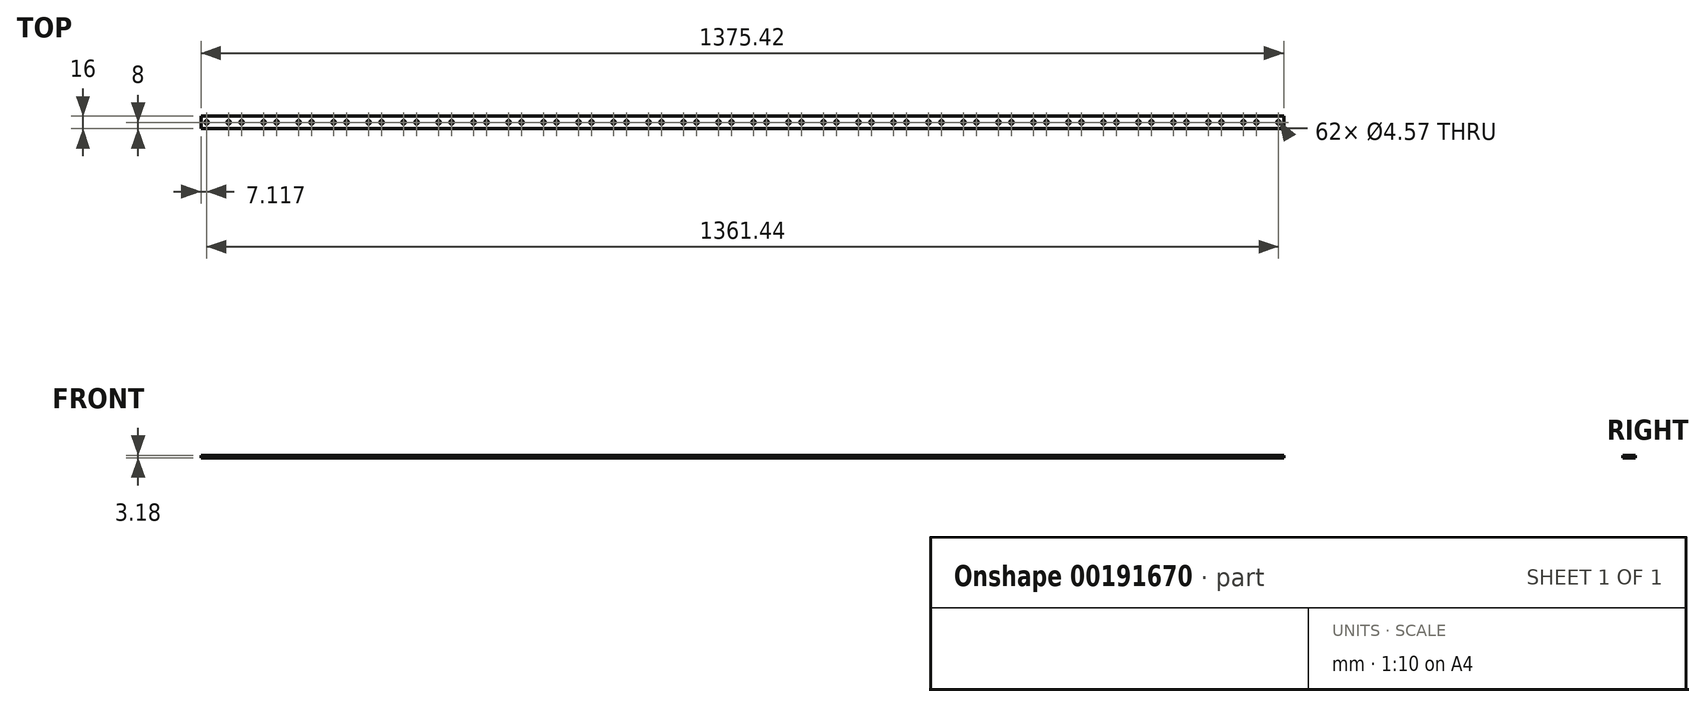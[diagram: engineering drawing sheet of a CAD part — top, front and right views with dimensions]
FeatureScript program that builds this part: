
annotation { "Feature Type Name" : "Feature", "Feature Type Description" : "" }
export const myFeature = defineFeature(function(context is Context, id is Id, definition is map)
    precondition{}
    {
        {
            var Q0;
            Q0=qCreatedBy(makeId("Top.planeOp"),FACE);
            var sketch = newSketch(context, id + "F0", { "sketchPlane" : qUnion([Q0])});
            skLineSegment(sketch, "E0.bottom", {"start": v(-687.7, 8) * mm, "end": v(687.7, 8) * mm});
            skLineSegment(sketch, "E0.top", {"start": v(-687.7, -8) * mm, "end": v(687.7, -8) * mm});
            skLineSegment(sketch, "E0.left", {"start": v(-687.7, 8) * mm, "end": v(-687.7, -8) * mm});
            skLineSegment(sketch, "E0.right", {"start": v(687.7, 8) * mm, "end": v(687.7, -8) * mm});
            skPoint(sketch, "E0.middle", {"position": v(0, 0) * mm});
            skLineSegment(sketch, "E1", {"start": v(-760.01, 0) * mm, "end": v(731.19, 0) * mm, "construction": true});
            skLineSegment(sketch, "E2.0", {"start": v(-680.6, 8) * mm, "end": v(-680.6, -8) * mm, "construction": true});
            skLineSegment(sketch, "E3.0", {"start": v(-652.65, 8) * mm, "end": v(-652.65, -8) * mm, "construction": true});
            skCircle(sketch, "E4", {"center": v(-680.6, 0) * mm, "radius": 2.29 * mm});
            skCircle(sketch, "E5", {"center": v(-652.65, 0) * mm, "radius": 2.29 * mm});
            skCircle(sketch, "E6.1.0.0", {"center": v(-636.14, 0) * mm, "radius": 2.29 * mm});
            skLineSegment(sketch, "E6.direction1", {"start": v(-652.65, 0) * mm, "end": v(-636.14, 0) * mm, "construction": true});
            skCircle(sketch, "E7.1.0.0", {"center": v(-608.2, 0) * mm, "radius": 2.29 * mm});
            skLineSegment(sketch, "E7.direction1", {"start": v(-636.14, 0) * mm, "end": v(-608.2, 0) * mm, "construction": true});
            skCircle(sketch, "E8.1.0.0", {"center": v(-591.7, 0) * mm, "radius": 2.29 * mm});
            skCircle(sketch, "E8.1.0.1", {"center": v(-563.75, 0) * mm, "radius": 2.29 * mm});
            skLineSegment(sketch, "E8.1.0.2", {"start": v(-591.7, 0) * mm, "end": v(-563.75, 0) * mm, "construction": true});
            skCircle(sketch, "E8.2.0.0", {"center": v(-547.24, 0) * mm, "radius": 2.29 * mm});
            skCircle(sketch, "E8.2.0.1", {"center": v(-519.3, 0) * mm, "radius": 2.29 * mm});
            skLineSegment(sketch, "E8.2.0.2", {"start": v(-547.24, 0) * mm, "end": v(-519.3, 0) * mm, "construction": true});
            skCircle(sketch, "E8.3.0.0", {"center": v(-502.8, 0) * mm, "radius": 2.29 * mm});
            skCircle(sketch, "E8.3.0.1", {"center": v(-474.85, 0) * mm, "radius": 2.29 * mm});
            skLineSegment(sketch, "E8.3.0.2", {"start": v(-502.8, 0) * mm, "end": v(-474.85, 0) * mm, "construction": true});
            skCircle(sketch, "E8.4.0.0", {"center": v(-458.34, 0) * mm, "radius": 2.29 * mm});
            skCircle(sketch, "E8.4.0.1", {"center": v(-430.4, 0) * mm, "radius": 2.29 * mm});
            skLineSegment(sketch, "E8.4.0.2", {"start": v(-458.34, 0) * mm, "end": v(-430.4, 0) * mm, "construction": true});
            skCircle(sketch, "E8.5.0.0", {"center": v(-413.9, 0) * mm, "radius": 2.29 * mm});
            skCircle(sketch, "E8.5.0.1", {"center": v(-385.95, 0) * mm, "radius": 2.29 * mm});
            skLineSegment(sketch, "E8.5.0.2", {"start": v(-413.9, 0) * mm, "end": v(-385.95, 0) * mm, "construction": true});
            skCircle(sketch, "E8.6.0.0", {"center": v(-369.44, 0) * mm, "radius": 2.29 * mm});
            skCircle(sketch, "E8.6.0.1", {"center": v(-341.5, 0) * mm, "radius": 2.29 * mm});
            skLineSegment(sketch, "E8.6.0.2", {"start": v(-369.44, 0) * mm, "end": v(-341.5, 0) * mm, "construction": true});
            skCircle(sketch, "E8.7.0.0", {"center": v(-325, 0) * mm, "radius": 2.29 * mm});
            skCircle(sketch, "E8.7.0.1", {"center": v(-297.05, 0) * mm, "radius": 2.29 * mm});
            skLineSegment(sketch, "E8.7.0.2", {"start": v(-325, 0) * mm, "end": v(-297.05, 0) * mm, "construction": true});
            skCircle(sketch, "E8.8.0.0", {"center": v(-280.54, 0) * mm, "radius": 2.29 * mm});
            skCircle(sketch, "E8.8.0.1", {"center": v(-252.6, 0) * mm, "radius": 2.29 * mm});
            skLineSegment(sketch, "E8.8.0.2", {"start": v(-280.54, 0) * mm, "end": v(-252.6, 0) * mm, "construction": true});
            skCircle(sketch, "E8.9.0.0", {"center": v(-236.1, 0) * mm, "radius": 2.29 * mm});
            skCircle(sketch, "E8.9.0.1", {"center": v(-208.15, 0) * mm, "radius": 2.29 * mm});
            skLineSegment(sketch, "E8.9.0.2", {"start": v(-236.1, 0) * mm, "end": v(-208.15, 0) * mm, "construction": true});
            skCircle(sketch, "E8.10.0.0", {"center": v(-191.64, 0) * mm, "radius": 2.29 * mm});
            skCircle(sketch, "E8.10.0.1", {"center": v(-163.7, 0) * mm, "radius": 2.29 * mm});
            skLineSegment(sketch, "E8.10.0.2", {"start": v(-191.64, 0) * mm, "end": v(-163.7, 0) * mm, "construction": true});
            skCircle(sketch, "E8.11.0.0", {"center": v(-147.2, 0) * mm, "radius": 2.29 * mm});
            skCircle(sketch, "E8.11.0.1", {"center": v(-119.25, 0) * mm, "radius": 2.29 * mm});
            skLineSegment(sketch, "E8.11.0.2", {"start": v(-147.2, 0) * mm, "end": v(-119.25, 0) * mm, "construction": true});
            skCircle(sketch, "E8.12.0.0", {"center": v(-102.74, 0) * mm, "radius": 2.29 * mm});
            skCircle(sketch, "E8.12.0.1", {"center": v(-74.8, 0) * mm, "radius": 2.29 * mm});
            skLineSegment(sketch, "E8.12.0.2", {"start": v(-102.74, 0) * mm, "end": v(-74.8, 0) * mm, "construction": true});
            skCircle(sketch, "E8.13.0.0", {"center": v(-58.3, 0) * mm, "radius": 2.29 * mm});
            skCircle(sketch, "E8.13.0.1", {"center": v(-30.35, 0) * mm, "radius": 2.29 * mm});
            skLineSegment(sketch, "E8.13.0.2", {"start": v(-58.3, 0) * mm, "end": v(-30.35, 0) * mm, "construction": true});
            skCircle(sketch, "E8.14.0.0", {"center": v(-13.84, 0) * mm, "radius": 2.29 * mm});
            skCircle(sketch, "E8.14.0.1", {"center": v(14.1, 0) * mm, "radius": 2.29 * mm});
            skLineSegment(sketch, "E8.14.0.2", {"start": v(-13.84, 0) * mm, "end": v(14.1, 0) * mm, "construction": true});
            skCircle(sketch, "E8.15.0.0", {"center": v(30.6, 0) * mm, "radius": 2.29 * mm});
            skCircle(sketch, "E8.15.0.1", {"center": v(58.55, 0) * mm, "radius": 2.29 * mm});
            skLineSegment(sketch, "E8.15.0.2", {"start": v(30.6, 0) * mm, "end": v(58.55, 0) * mm, "construction": true});
            skCircle(sketch, "E8.16.0.0", {"center": v(75.06, 0) * mm, "radius": 2.29 * mm});
            skCircle(sketch, "E8.16.0.1", {"center": v(103, 0) * mm, "radius": 2.29 * mm});
            skLineSegment(sketch, "E8.16.0.2", {"start": v(75.06, 0) * mm, "end": v(103, 0) * mm, "construction": true});
            skCircle(sketch, "E8.17.0.0", {"center": v(119.5, 0) * mm, "radius": 2.29 * mm});
            skCircle(sketch, "E8.17.0.1", {"center": v(147.45, 0) * mm, "radius": 2.29 * mm});
            skLineSegment(sketch, "E8.17.0.2", {"start": v(119.5, 0) * mm, "end": v(147.45, 0) * mm, "construction": true});
            skCircle(sketch, "E8.18.0.0", {"center": v(163.96, 0) * mm, "radius": 2.29 * mm});
            skCircle(sketch, "E8.18.0.1", {"center": v(191.9, 0) * mm, "radius": 2.29 * mm});
            skLineSegment(sketch, "E8.18.0.2", {"start": v(163.96, 0) * mm, "end": v(191.9, 0) * mm, "construction": true});
            skCircle(sketch, "E8.19.0.0", {"center": v(208.4, 0) * mm, "radius": 2.29 * mm});
            skCircle(sketch, "E8.19.0.1", {"center": v(236.35, 0) * mm, "radius": 2.29 * mm});
            skLineSegment(sketch, "E8.19.0.2", {"start": v(208.4, 0) * mm, "end": v(236.35, 0) * mm, "construction": true});
            skCircle(sketch, "E8.20.0.0", {"center": v(252.86, 0) * mm, "radius": 2.29 * mm});
            skCircle(sketch, "E8.20.0.1", {"center": v(280.8, 0) * mm, "radius": 2.29 * mm});
            skLineSegment(sketch, "E8.20.0.2", {"start": v(252.86, 0) * mm, "end": v(280.8, 0) * mm, "construction": true});
            skCircle(sketch, "E8.21.0.0", {"center": v(297.3, 0) * mm, "radius": 2.29 * mm});
            skCircle(sketch, "E8.21.0.1", {"center": v(325.25, 0) * mm, "radius": 2.29 * mm});
            skLineSegment(sketch, "E8.21.0.2", {"start": v(297.3, 0) * mm, "end": v(325.25, 0) * mm, "construction": true});
            skCircle(sketch, "E8.22.0.0", {"center": v(341.76, 0) * mm, "radius": 2.29 * mm});
            skCircle(sketch, "E8.22.0.1", {"center": v(369.7, 0) * mm, "radius": 2.29 * mm});
            skLineSegment(sketch, "E8.22.0.2", {"start": v(341.76, 0) * mm, "end": v(369.7, 0) * mm, "construction": true});
            skCircle(sketch, "E8.23.0.0", {"center": v(386.2, 0) * mm, "radius": 2.29 * mm});
            skCircle(sketch, "E8.23.0.1", {"center": v(414.15, 0) * mm, "radius": 2.29 * mm});
            skLineSegment(sketch, "E8.23.0.2", {"start": v(386.2, 0) * mm, "end": v(414.15, 0) * mm, "construction": true});
            skCircle(sketch, "E8.24.0.0", {"center": v(430.66, 0) * mm, "radius": 2.29 * mm});
            skCircle(sketch, "E8.24.0.1", {"center": v(458.6, 0) * mm, "radius": 2.29 * mm});
            skLineSegment(sketch, "E8.24.0.2", {"start": v(430.66, 0) * mm, "end": v(458.6, 0) * mm, "construction": true});
            skCircle(sketch, "E8.25.0.0", {"center": v(475.1, 0) * mm, "radius": 2.29 * mm});
            skCircle(sketch, "E8.25.0.1", {"center": v(503.05, 0) * mm, "radius": 2.29 * mm});
            skLineSegment(sketch, "E8.25.0.2", {"start": v(475.1, 0) * mm, "end": v(503.05, 0) * mm, "construction": true});
            skCircle(sketch, "E8.26.0.0", {"center": v(519.56, 0) * mm, "radius": 2.29 * mm});
            skCircle(sketch, "E8.26.0.1", {"center": v(547.5, 0) * mm, "radius": 2.29 * mm});
            skLineSegment(sketch, "E8.26.0.2", {"start": v(519.56, 0) * mm, "end": v(547.5, 0) * mm, "construction": true});
            skCircle(sketch, "E8.27.0.0", {"center": v(564, 0) * mm, "radius": 2.29 * mm});
            skCircle(sketch, "E8.27.0.1", {"center": v(591.95, 0) * mm, "radius": 2.29 * mm});
            skLineSegment(sketch, "E8.27.0.2", {"start": v(564, 0) * mm, "end": v(591.95, 0) * mm, "construction": true});
            skCircle(sketch, "E8.28.0.0", {"center": v(608.46, 0) * mm, "radius": 2.29 * mm});
            skCircle(sketch, "E8.28.0.1", {"center": v(636.4, 0) * mm, "radius": 2.29 * mm});
            skLineSegment(sketch, "E8.28.0.2", {"start": v(608.46, 0) * mm, "end": v(636.4, 0) * mm, "construction": true});
            skCircle(sketch, "E8.29.0.0", {"center": v(652.9, 0) * mm, "radius": 2.29 * mm});
            skCircle(sketch, "E8.29.0.1", {"center": v(680.85, 0) * mm, "radius": 2.29 * mm});
            skLineSegment(sketch, "E8.29.0.2", {"start": v(652.9, 0) * mm, "end": v(680.85, 0) * mm, "construction": true});
            skLineSegment(sketch, "E8.direction1", {"start": v(-636.14, 0) * mm, "end": v(-591.7, 0) * mm, "construction": true});
            skSolve(sketch);
        }
        {
            var Q0;
            Q0=makeQuery(id+"F0.imprint","IMPRINT",FACE,{"disambiguationData":[TD([[makeQuery(id+"F0.imprint","IMPRINT",EDGE,{"derivedFrom":sQuery(id+"F0.wireOp",EDGE,"E0.bottom")}),-1.0]])]});
            extrude(context, id + "F1", {"entities" : qUnion([Q0]), "depth" : 3.17 * mm});
        }
    });
